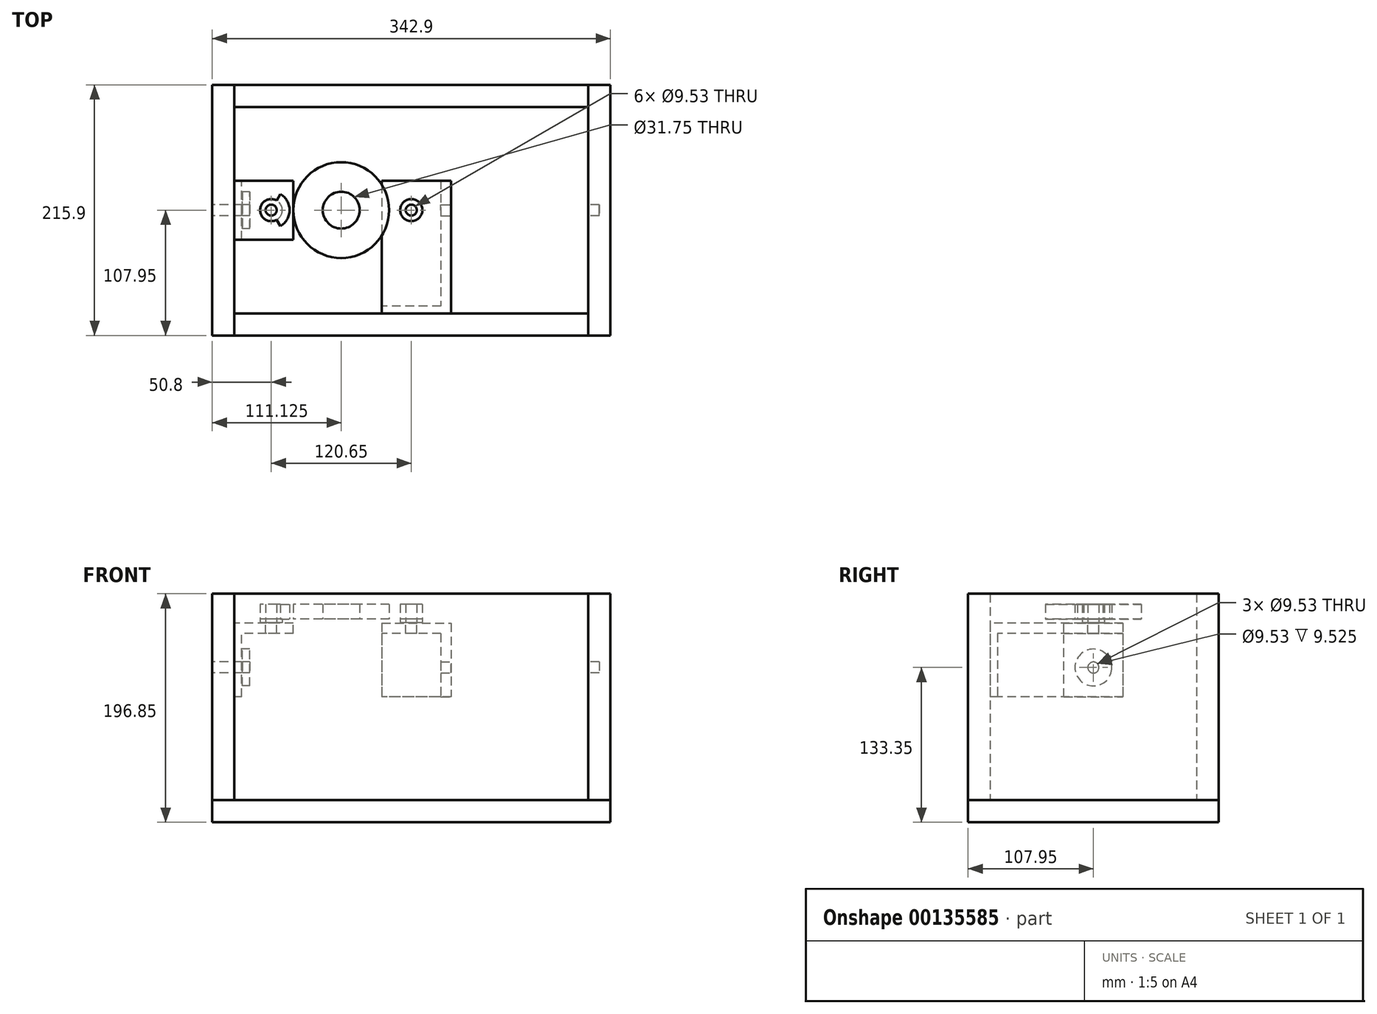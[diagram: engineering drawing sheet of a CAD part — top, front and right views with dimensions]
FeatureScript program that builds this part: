
annotation { "Feature Type Name" : "Feature", "Feature Type Description" : "" }
export const myFeature = defineFeature(function(context is Context, id is Id, definition is map)
    precondition{}
    {
        {
            var Q0;
            Q0=qCreatedBy(makeId("Top.planeOp"),FACE);
            var sketch = newSketch(context, id + "F0", { "sketchPlane" : qUnion([Q0])});
            skLineSegment(sketch, "E0.bottom", {"start": v(-152.4, 88.9) * mm, "end": v(152.4, 88.9) * mm});
            skLineSegment(sketch, "E0.top", {"start": v(-152.4, -88.9) * mm, "end": v(152.4, -88.9) * mm});
            skLineSegment(sketch, "E0.left", {"start": v(-152.4, 88.9) * mm, "end": v(-152.4, -88.9) * mm});
            skLineSegment(sketch, "E0.right", {"start": v(152.4, 88.9) * mm, "end": v(152.4, -88.9) * mm});
            skLineSegment(sketch, "E1.bottom", {"start": v(152.4, 107.95) * mm, "end": v(171.45, 107.95) * mm});
            skLineSegment(sketch, "E1.top", {"start": v(152.4, -107.95) * mm, "end": v(171.45, -107.95) * mm});
            skLineSegment(sketch, "E1.left", {"start": v(152.4, 107.95) * mm, "end": v(152.4, -107.95) * mm});
            skLineSegment(sketch, "E1.right", {"start": v(171.45, 107.95) * mm, "end": v(171.45, -107.95) * mm});
            skLineSegment(sketch, "E2", {"start": v(152.4, 107.95) * mm, "end": v(152.4, 0) * mm});
            skLineSegment(sketch, "E3", {"start": v(152.4, 88.9) * mm, "end": v(152.4, 0) * mm});
            skLineSegment(sketch, "E4.bottom", {"start": v(-171.45, 107.95) * mm, "end": v(-152.4, 107.95) * mm});
            skLineSegment(sketch, "E4.top", {"start": v(-171.45, -107.95) * mm, "end": v(-152.4, -107.95) * mm});
            skLineSegment(sketch, "E4.left", {"start": v(-171.45, 107.95) * mm, "end": v(-171.45, -107.95) * mm});
            skLineSegment(sketch, "E4.right", {"start": v(-152.4, 107.95) * mm, "end": v(-152.4, -107.95) * mm});
            skLineSegment(sketch, "E5", {"start": v(-171.45, 107.95) * mm, "end": v(-171.45, 0) * mm});
            skLineSegment(sketch, "E6", {"start": v(-152.4, 107.95) * mm, "end": v(-152.4, 0) * mm});
            skLineSegment(sketch, "E7", {"start": v(-152.4, 88.9) * mm, "end": v(-152.4, 0) * mm});
            skLineSegment(sketch, "E8.bottom", {"start": v(-152.4, 107.95) * mm, "end": v(152.4, 107.95) * mm});
            skLineSegment(sketch, "E8.left", {"start": v(-152.4, 107.95) * mm, "end": v(-152.4, 88.9) * mm});
            skLineSegment(sketch, "E8.right", {"start": v(152.4, 107.95) * mm, "end": v(152.4, 88.9) * mm});
            skLineSegment(sketch, "E9.bottom", {"start": v(-152.4, -107.95) * mm, "end": v(152.4, -107.95) * mm});
            skLineSegment(sketch, "E9.left", {"start": v(-152.4, -107.95) * mm, "end": v(-152.4, -88.9) * mm});
            skLineSegment(sketch, "E9.right", {"start": v(152.4, -107.95) * mm, "end": v(152.4, -88.9) * mm});
            skLineSegment(sketch, "E10", {"start": v(0, 88.9) * mm, "end": v(0, -88.9) * mm});
            skPoint(sketch, "E11", {"position": v(0, 0) * mm});
            skSolve(sketch);
        }
        {
            var Q0;
            Q0=makeQuery(id+"F0.imprint","IMPRINT",FACE,{"disambiguationData":[TD([[makeQuery(id+"F0.imprint","IMPRINT",EDGE,{"derivedFrom":sQuery(id+"F0.wireOp",EDGE,"E4.bottom")}),-1.0]])]});
            extrude(context, id + "F1", {"entities" : qUnion([Q0]), "depth" : 177.8 * mm});
        }
        {
            var Q0;
            Q0=makeQuery(id+"F0.imprint","IMPRINT",FACE,{"disambiguationData":[TD([[makeQuery(id+"F0.imprint","IMPRINT",EDGE,{"derivedFrom":sQuery(id+"F0.wireOp",EDGE,"E1.bottom")}),-1.0]])]});
            extrude(context, id + "F2", {"entities" : qUnion([Q0]), "depth" : 177.8 * mm});
        }
        {
            var Q0;
            Q0=makeQuery(id+"F0.imprint","IMPRINT",FACE,{"disambiguationData":[TD([[makeQuery(id+"F0.imprint","IMPRINT",EDGE,{"derivedFrom":sQuery(id+"F0.wireOp",EDGE,"E8.bottom")}),-1.0]])]});
            extrude(context, id + "F3", {"entities" : qUnion([Q0]), "depth" : 177.8 * mm});
        }
        {
            var Q0;
            Q0=makeQuery(id+"F0.imprint","IMPRINT",FACE,{"disambiguationData":[TD([[makeQuery(id+"F0.imprint","IMPRINT",EDGE,{"derivedFrom":sQuery(id+"F0.wireOp",EDGE,"E9.bottom")}),1.0]])]});
            extrude(context, id + "F4", {"entities" : qUnion([Q0]), "depth" : 177.8 * mm});
        }
        {
            var Q0;
            Q0=qCreatedBy(makeId("Top.planeOp"),FACE);
            var sketch = newSketch(context, id + "F5", { "sketchPlane" : qUnion([Q0])});
            skLineSegment(sketch, "E12.bottom", {"start": v(-171.45, -107.95) * mm, "end": v(171.45, -107.95) * mm});
            skLineSegment(sketch, "E12.top", {"start": v(-171.45, 107.95) * mm, "end": v(171.45, 107.95) * mm});
            skLineSegment(sketch, "E12.left", {"start": v(-171.45, -107.95) * mm, "end": v(-171.45, 107.95) * mm});
            skLineSegment(sketch, "E12.right", {"start": v(171.45, -107.95) * mm, "end": v(171.45, 107.95) * mm});
            skSolve(sketch);
        }
        {
            var Q0;
            Q0=qSketchRegion(id+"F5",true);
            extrude(context, id + "F6", {"entities" : qUnion([Q0]), "oppositeDirection" : true, "depth" : 19.05 * mm});
        }
        {
            var Q0;
            Q0=makeQuery(id+"F1.opExtrude","SWEPT_FACE",FACE,{"disambiguationData":[OSD([sQuery(id+"F0.wireOp",EDGE,"E4.left"),sQuery(id+"F0.wireOp",EDGE,"E5")])]});
            var sketch = newSketch(context, id + "F7", { "sketchPlane" : qUnion([Q0])});
            skLineSegment(sketch, "E13", {"start": v(0, 0) * mm, "end": v(0, 114.3) * mm, "construction": true});
            skCircle(sketch, "E14", {"center": v(0, 114.3) * mm, "radius": 4.76 * mm});
            skSolve(sketch);
        }
        {
            var Q0;
            Q0=makeQuery(id+"F7.imprint","IMPRINT",FACE,{"disambiguationData":[TD([[makeQuery(id+"F7.imprint","IMPRINT",EDGE,{"derivedFrom":sQuery(id+"F7.wireOp",EDGE,"E14")}),1.0]])]});
            var Q1;
            Q1=sQuery(id+"F7.wireOp",EDGE,"E14");
            extrude(context, id + "F8", {"entities" : qUnion([Q0]), "operationType" : NewBodyOperationType.REMOVE, "surfaceEntities" : qUnion([Q1]), "oppositeDirection" : true, "depth" : 19.05 * mm});
        }
        {
            var Q0;
            Q0=makeQuery(id+"F2.opExtrude","SWEPT_FACE",FACE,{"disambiguationData":[OSD([sQuery(id+"F0.wireOp",EDGE,"E1.left"),sQuery(id+"F0.wireOp",EDGE,"E3"),sQuery(id+"F0.wireOp",EDGE,"E8.right"),sQuery(id+"F0.wireOp",EDGE,"E9.right")])]});
            var sketch = newSketch(context, id + "F9", { "sketchPlane" : qUnion([Q0])});
            skCircle(sketch, "E15.0", {"center": v(0, 114.3) * mm, "radius": 4.76 * mm});
            skSolve(sketch);
        }
        {
            var Q0;
            Q0=makeQuery(id+"F9.imprint","IMPRINT",FACE,{"disambiguationData":[TD([[makeQuery(id+"F9.imprint","IMPRINT",EDGE,{"derivedFrom":sQuery(id+"F9.wireOp",EDGE,"E15.0")}),1.0]])]});
            extrude(context, id + "F10", {"entities" : qUnion([Q0]), "operationType" : NewBodyOperationType.REMOVE, "oppositeDirection" : true, "depth" : 9.52 * mm});
        }
        {
            var Q0;
            Q0=makeQuery(id+"F1.opExtrude","SWEPT_FACE",FACE,{"disambiguationData":[OSD([sQuery(id+"F0.wireOp",EDGE,"E4.right"),sQuery(id+"F0.wireOp",EDGE,"E7"),sQuery(id+"F0.wireOp",EDGE,"E8.left"),sQuery(id+"F0.wireOp",EDGE,"E9.left")])]});
            var sketch = newSketch(context, id + "F11", { "sketchPlane" : qUnion([Q0])});
            skCircle(sketch, "E16.0", {"center": v(0, 114.3) * mm, "radius": 4.76 * mm, "construction": true});
            skLineSegment(sketch, "E17", {"start": v(0, 114.3) * mm, "end": v(-25.4, 114.3) * mm, "construction": true});
            skLineSegment(sketch, "E18", {"start": v(0, 114.3) * mm, "end": v(25.4, 114.3) * mm, "construction": true});
            skLineSegment(sketch, "E19", {"start": v(-25.4, 114.3) * mm, "end": v(-25.4, 88.9) * mm, "construction": true});
            skLineSegment(sketch, "E20", {"start": v(-25.4, 114.3) * mm, "end": v(-25.4, 152.4) * mm, "construction": true});
            skLineSegment(sketch, "E21.MirrorCS", {"start": v(25.4, 114.3) * mm, "end": v(25.4, 152.4) * mm, "construction": true});
            skLineSegment(sketch, "E22.MirrorCS", {"start": v(25.4, 114.3) * mm, "end": v(25.4, 88.9) * mm, "construction": true});
            skLineSegment(sketch, "E23", {"start": v(-25.4, 152.4) * mm, "end": v(25.4, 152.4) * mm, "construction": true});
            skLineSegment(sketch, "E24", {"start": v(-25.4, 88.9) * mm, "end": v(25.4, 88.9) * mm, "construction": true});
            skLineSegment(sketch, "E25.bottom", {"start": v(-25.4, 88.9) * mm, "end": v(25.4, 88.9) * mm});
            skLineSegment(sketch, "E25.top", {"start": v(-25.4, 152.4) * mm, "end": v(25.4, 152.4) * mm});
            skLineSegment(sketch, "E25.left", {"start": v(-25.4, 88.9) * mm, "end": v(-25.4, 152.4) * mm});
            skLineSegment(sketch, "E25.right", {"start": v(25.4, 88.9) * mm, "end": v(25.4, 152.4) * mm});
            skLineSegment(sketch, "E26", {"start": v(-25.4, 152.4) * mm, "end": v(-25.4, 143.5) * mm, "construction": true});
            skLineSegment(sketch, "E27", {"start": v(-25.4, 143.5) * mm, "end": v(25.4, 143.5) * mm});
            skSolve(sketch);
        }
        {
            var Q0;
            {var subQ2=sQuery(id+"F11.wireOp",EDGE,"E25.bottom");Q0=makeQuery(id+"F11.imprint","IMPRINT",FACE,{"disambiguationData":[TD([[makeQuery(id+"F11.imprint","IMPRINT",EDGE,{"derivedFrom":subQ2}),1.0]])]});}
            extrude(context, id + "F12", {"entities" : qUnion([Q0]), "operationType" : NewBodyOperationType.ADD, "depth" : 6.35 * mm});
        }
        {
            var Q0;
            {var subQ0=sQuery(id+"F11.wireOp",EDGE,"E25.top");Q0=makeQuery(id+"F11.imprint","IMPRINT",FACE,{"disambiguationData":[TD([[makeQuery(id+"F11.imprint","IMPRINT",EDGE,{"derivedFrom":subQ0}),-1.0]])]});}
            extrude(context, id + "F13", {"entities" : qUnion([Q0]), "operationType" : NewBodyOperationType.ADD, "depth" : 50.8 * mm});
        }
        {
            var Q0;
            Q0=makeQuery(id+"F12.opExtrude","CAP_FACE",FACE,{"disambiguationData":[OSD([sQuery(id+"F7.wireOp",EDGE,"E14"),sQuery(id+"F11.wireOp",EDGE,"E25.bottom"),sQuery(id+"F11.wireOp",EDGE,"E25.left"),sQuery(id+"F11.wireOp",EDGE,"E25.right"),sQuery(id+"F11.wireOp",EDGE,"E27")])],"isStart":false});
            var sketch = newSketch(context, id + "F14", { "sketchPlane" : qUnion([Q0])});
            skCircle(sketch, "E28.0", {"center": v(0, 114.3) * mm, "radius": 4.76 * mm, "construction": true});
            skCircle(sketch, "E29", {"center": v(0, 114.3) * mm, "radius": 15.88 * mm});
            skCircle(sketch, "E30", {"center": v(0, 82.55) * mm, "radius": 4.76 * mm});
            skCircle(sketch, "E31", {"center": v(0, 82.55) * mm, "radius": 15.88 * mm});
            skLineSegment(sketch, "E32", {"start": v(0, 114.3) * mm, "end": v(0, 82.55) * mm, "construction": true});
            skLineSegment(sketch, "E33", {"start": v(-4.76, 114.33) * mm, "end": v(4.76, 114.33) * mm, "construction": true});
            skLineSegment(sketch, "E34", {"start": v(0, 82.55) * mm, "end": v(0, 50.8) * mm, "construction": true});
            skCircle(sketch, "E35", {"center": v(0, 50.8) * mm, "radius": 4.76 * mm});
            skCircle(sketch, "E36", {"center": v(0, 50.8) * mm, "radius": 15.88 * mm});
            skSolve(sketch);
        }
        {
            var Q0;
            Q0=makeQuery(id+"F14.imprint","IMPRINT",FACE,{"disambiguationData":[TD([[makeQuery(id+"F14.imprint","IMPRINT",EDGE,{"derivedFrom":sQuery(id+"F14.wireOp",EDGE,"E29")}),1.0]])]});
            var Q1;
            Q1=makeQuery(id+"F14.imprint","IMPRINT",FACE,{"disambiguationData":[TD([[makeQuery(id+"F14.imprint","IMPRINT",EDGE,{"derivedFrom":sQuery(id+"F14.wireOp",EDGE,"wCvrm9ek-Vla4-kLHZ-fckN-ywa5dthquzuu")}),-1.0]])]});
            var Q2;
            {var subQ0=sQuery(id+"F14.wireOp",EDGE,"TcqK1HJN-8NVO-TRNo-AAgI-cdNEvH082vga");var subQ1=makeQuery(id+"F12.opExtrude","CAP_EDGE",EDGE,{"disambiguationData":[OSD([sQuery(id+"F11.wireOp",EDGE,"E25.bottom")])],"isStart":false});var subQ2=makeQuery(id+"F14.imprint","INTERSECT",VERTEX,{"disambiguationData":[OD(0.0)],"derivedFrom":[subQ1,subQ0]});Q2=makeQuery(id+"F14.imprint","IMPRINT",FACE,{"disambiguationData":[TD([[makeQuery(id+"F14.imprint","IMPRINT",EDGE,{"disambiguationData":[TD([[subQ2,1.0]])],"derivedFrom":subQ0}),1.0]])]});}
            var Q3;
            Q3=makeQuery(id+"F14.imprint","IMPRINT",FACE,{"disambiguationData":[TD([[makeQuery(id+"F14.imprint","IMPRINT",EDGE,{"derivedFrom":sQuery(id+"F14.wireOp",EDGE,"75hCYlV7-Y9NR-4qaa-elEN-DsRLMhdoIlUx")}),1.0]])]});
            extrude(context, id + "F15", {"entities" : qUnion([Q0, Q1, Q2, Q3]), "depth" : 6.86 * mm, "hasSecondDirection" : true, "secondDirectionOppositeDirection" : false, "secondDirectionDepth" : 0.5 * mm});
        }
        {
            var Q0;
            Q0=makeQuery(id+"F13.opExtrude","SWEPT_FACE",FACE,{"disambiguationData":[OSD([sQuery(id+"F11.wireOp",EDGE,"E25.top")])]});
            var sketch = newSketch(context, id + "F16", { "sketchPlane" : qUnion([Q0])});
            skLineSegment(sketch, "E37", {"start": v(-152.4, 0) * mm, "end": v(-101.6, 0) * mm, "construction": true});
            skLineSegment(sketch, "E38", {"start": v(-101.6, 0) * mm, "end": v(-127, 0) * mm, "construction": true});
            skLineSegment(sketch, "E39", {"start": v(-127, 0) * mm, "end": v(-114.3, 0) * mm, "construction": true});
            skLineSegment(sketch, "E40", {"start": v(-114.3, 0) * mm, "end": v(-120.65, 0) * mm, "construction": true});
            skCircle(sketch, "E41", {"center": v(-120.65, 0) * mm, "radius": 4.76 * mm});
            skSolve(sketch);
        }
        {
            var Q0;
            Q0=makeQuery(id+"F16.imprint","IMPRINT",FACE,{"disambiguationData":[TD([[makeQuery(id+"F16.imprint","IMPRINT",EDGE,{"derivedFrom":sQuery(id+"F16.wireOp",EDGE,"E41")}),1.0]])]});
            var Q1;
            Q1=sQuery(id+"F16.wireOp",EDGE,"E41");
            extrude(context, id + "F17", {"entities" : qUnion([Q0]), "operationType" : NewBodyOperationType.REMOVE, "surfaceEntities" : qUnion([Q1]), "oppositeDirection" : true, "depth" : 25.4 * mm});
        }
        {
            var Q0;
            Q0=makeQuery(id+"F4.opExtrude","SWEPT_FACE",FACE,{"disambiguationData":[OSD([sQuery(id+"F0.wireOp",EDGE,"E0.top")])]});
            var sketch = newSketch(context, id + "F18", { "sketchPlane" : qUnion([Q0])});
            skLineSegment(sketch, "E42.0.0", {"start": v(152.4, 88.9) * mm, "end": v(152.4, 152.4) * mm, "construction": true});
            skLineSegment(sketch, "E42.0.1", {"start": v(152.4, 152.4) * mm, "end": v(101.6, 152.4) * mm, "construction": true});
            skLineSegment(sketch, "E42.0.2", {"start": v(101.6, 152.4) * mm, "end": v(101.6, 143.5) * mm, "construction": true});
            skLineSegment(sketch, "E42.0.3", {"start": v(101.6, 143.5) * mm, "end": v(146.05, 143.5) * mm, "construction": true});
            skLineSegment(sketch, "E42.0.4", {"start": v(146.05, 143.5) * mm, "end": v(146.05, 88.9) * mm, "construction": true});
            skLineSegment(sketch, "E42.0.5", {"start": v(146.05, 88.9) * mm, "end": v(152.4, 88.9) * mm, "construction": true});
            skLineSegment(sketch, "E43", {"start": v(152.4, 152.4) * mm, "end": v(-25.4, 152.4) * mm, "construction": true});
            skLineSegment(sketch, "E44.bottom", {"start": v(-25.4, 152.4) * mm, "end": v(25.4, 152.4) * mm});
            skLineSegment(sketch, "E44.top", {"start": v(-25.4, 88.9) * mm, "end": v(25.4, 88.9) * mm});
            skLineSegment(sketch, "E44.left", {"start": v(-25.4, 152.4) * mm, "end": v(-25.4, 88.9) * mm});
            skLineSegment(sketch, "E44.right", {"start": v(25.4, 152.4) * mm, "end": v(25.4, 88.9) * mm});
            skLineSegment(sketch, "E45.top", {"start": v(-25.4, 143.5) * mm, "end": v(25.4, 143.5) * mm});
            skLineSegment(sketch, "E45.left", {"start": v(-25.4, 152.4) * mm, "end": v(-25.4, 143.5) * mm});
            skLineSegment(sketch, "E45.right", {"start": v(25.4, 152.4) * mm, "end": v(25.4, 143.5) * mm});
            skLineSegment(sketch, "E46.bottom", {"start": v(-25.4, 152.4) * mm, "end": v(-34.3, 152.4) * mm});
            skLineSegment(sketch, "E46.top", {"start": v(-25.4, 88.9) * mm, "end": v(-34.3, 88.9) * mm});
            skLineSegment(sketch, "E46.right", {"start": v(-34.3, 152.4) * mm, "end": v(-34.3, 88.9) * mm});
            skSolve(sketch);
        }
        {
            var Q0;
            {var subQ0=sQuery(id+"F18.wireOp",EDGE,"E44.top");Q0=makeQuery(id+"F18.imprint","IMPRINT",FACE,{"disambiguationData":[TD([[makeQuery(id+"F18.imprint","IMPRINT",EDGE,{"derivedFrom":subQ0}),1.0]])]});}
            extrude(context, id + "F19", {"entities" : qUnion([Q0]), "operationType" : NewBodyOperationType.ADD, "depth" : 6.35 * mm});
        }
        {
            var Q0;
            {var subQ3=sQuery(id+"F18.wireOp",EDGE,"E46.bottom");Q0=makeQuery(id+"F18.imprint","IMPRINT",FACE,{"disambiguationData":[TD([[makeQuery(id+"F18.imprint","IMPRINT",EDGE,{"derivedFrom":subQ3}),1.0]])]});}
            var Q1;
            {var subQ0=sQuery(id+"F18.wireOp",EDGE,"E44.bottom");Q1=makeQuery(id+"F18.imprint","IMPRINT",FACE,{"disambiguationData":[TD([[makeQuery(id+"F18.imprint","IMPRINT",EDGE,{"derivedFrom":subQ0}),-1.0]])]});}
            extrude(context, id + "F20", {"entities" : qUnion([Q0, Q1]), "operationType" : NewBodyOperationType.ADD, "depth" : 114.3 * mm});
        }
        {
            var Q0;
            Q0=makeQuery(id+"F20.opExtrude","SWEPT_FACE",FACE,{"disambiguationData":[OSD([sQuery(id+"F18.wireOp",EDGE,"E46.right")])]});
            var sketch = newSketch(context, id + "F21", { "sketchPlane" : qUnion([Q0])});
            skCircle(sketch, "E47.0", {"center": v(0, 114.3) * mm, "radius": 4.76 * mm});
            skSolve(sketch);
        }
        {
            var Q0;
            Q0=makeQuery(id+"F21.imprint","IMPRINT",FACE,{"disambiguationData":[TD([[makeQuery(id+"F21.imprint","IMPRINT",EDGE,{"derivedFrom":sQuery(id+"F21.wireOp",EDGE,"E47.0")}),1.0]])]});
            var Q1;
            Q1=sQuery(id+"F21.wireOp",EDGE,"E47.0");
            extrude(context, id + "F22", {"entities" : qUnion([Q0]), "operationType" : NewBodyOperationType.REMOVE, "surfaceEntities" : qUnion([Q1]), "oppositeDirection" : true, "depth" : 25.4 * mm});
        }
        {
            var Q0;
            Q0=makeQuery(id+"F20.opExtrude","SWEPT_FACE",FACE,{"disambiguationData":[OSD([sQuery(id+"F18.wireOp",EDGE,"E44.bottom"),sQuery(id+"F18.wireOp",EDGE,"E46.bottom")])]});
            var sketch = newSketch(context, id + "F23", { "sketchPlane" : qUnion([Q0])});
            skCircle(sketch, "E48.0", {"center": v(-120.65, 0) * mm, "radius": 4.76 * mm, "construction": true});
            skLineSegment(sketch, "E49", {"start": v(-120.65, 0) * mm, "end": v(0, 0) * mm, "construction": true});
            skCircle(sketch, "E50", {"center": v(0, 0) * mm, "radius": 4.76 * mm});
            skSolve(sketch);
        }
        {
            var Q0;
            Q0=makeQuery(id+"F23.imprint","IMPRINT",FACE,{"disambiguationData":[TD([[makeQuery(id+"F23.imprint","IMPRINT",EDGE,{"derivedFrom":sQuery(id+"F23.wireOp",EDGE,"E50")}),1.0]])]});
            var Q1;
            Q1=sQuery(id+"F23.wireOp",EDGE,"E50");
            extrude(context, id + "F24", {"entities" : qUnion([Q0]), "operationType" : NewBodyOperationType.REMOVE, "surfaceEntities" : qUnion([Q1]), "oppositeDirection" : true, "depth" : 25.4 * mm});
        }
        {
            var Q0;
            Q0=makeQuery(id+"F20.opExtrude","SWEPT_FACE",FACE,{"disambiguationData":[OSD([sQuery(id+"F18.wireOp",EDGE,"E44.bottom"),sQuery(id+"F18.wireOp",EDGE,"E46.bottom")])]});
            var sketch = newSketch(context, id + "F25", { "sketchPlane" : qUnion([Q0])});
            skCircle(sketch, "E51.0", {"center": v(-120.65, 0) * mm, "radius": 4.76 * mm});
            skCircle(sketch, "E52.0", {"center": v(0, 0) * mm, "radius": 4.76 * mm});
            skLineSegment(sketch, "E53", {"start": v(-120.65, 0) * mm, "end": v(0, 0) * mm, "construction": true});
            skLineSegment(sketch, "E54", {"start": v(-60.32, 0) * mm, "end": v(-60.32, 25.4) * mm, "construction": true});
            skCircle(sketch, "E55", {"center": v(0, 0) * mm, "radius": 9.53 * mm});
            skCircle(sketch, "E56.MirrorC", {"center": v(-120.65, 0) * mm, "radius": 9.53 * mm});
            skSolve(sketch);
        }
        {
            var Q0;
            Q0=makeQuery(id+"F25.imprint","IMPRINT",FACE,{"disambiguationData":[TD([[makeQuery(id+"F25.imprint","IMPRINT",EDGE,{"derivedFrom":sQuery(id+"F25.wireOp",EDGE,"E51.0")}),-1.0]])]});
            var Q1;
            Q1=makeQuery(id+"F25.imprint","IMPRINT",FACE,{"disambiguationData":[TD([[makeQuery(id+"F25.imprint","IMPRINT",EDGE,{"derivedFrom":sQuery(id+"F25.wireOp",EDGE,"E52.0")}),-1.0]])]});
            var Q2;
            Q2=sQuery(id+"F25.wireOp",EDGE,"E56.MirrorC");
            var Q3;
            Q3=sQuery(id+"F25.wireOp",EDGE,"E55");
            extrude(context, id + "F26", {"entities" : qUnion([Q0, Q1]), "operationType" : NewBodyOperationType.ADD, "surfaceEntities" : qUnion([Q2, Q3]), "depth" : 3.68 * mm, "hasSecondDirection" : true, "secondDirectionOppositeDirection" : false, "secondDirectionDepth" : 0.5 * mm});
        }
        {
            var Q0;
            Q0=makeQuery(id+"F26.opExtrude","CAP_FACE",FACE,{"disambiguationData":[OSD([sQuery(id+"F25.wireOp",EDGE,"E51.0"),sQuery(id+"F25.wireOp",EDGE,"E56.MirrorC")])],"isStart":false});
            var sketch = newSketch(context, id + "F27", { "sketchPlane" : qUnion([Q0])});
            skCircle(sketch, "E57.0", {"center": v(-120.65, 0) * mm, "radius": 4.76 * mm, "construction": true});
            skCircle(sketch, "E58.0", {"center": v(0, 0) * mm, "radius": 4.76 * mm, "construction": true});
            skLineSegment(sketch, "E59", {"start": v(-120.65, 0) * mm, "end": v(0, 0) * mm, "construction": true});
            skLineSegment(sketch, "E60", {"start": v(-60.32, 0) * mm, "end": v(-60.32, 25.4) * mm, "construction": true});
            skArc(sketch, "E61", {"start": v(-112.71, -13.75) * mm, "mid": v(-104.77, 0) * mm, "end": v(-112.71, 13.75) * mm});
            skLineSegment(sketch, "E62", {"start": v(-120.65, 0) * mm, "end": v(-120.65, 9.53) * mm, "construction": true});
            skLineSegment(sketch, "E63", {"start": v(-120.65, 0) * mm, "end": v(-120.65, -9.53) * mm, "construction": true});
            skLineSegment(sketch, "E64", {"start": v(-120.65, 0) * mm, "end": v(-112.71, 13.75) * mm, "construction": true});
            skLineSegment(sketch, "E65", {"start": v(-120.65, 0) * mm, "end": v(-112.71, -13.75) * mm, "construction": true});
            skLineSegment(sketch, "E66", {"start": v(-112.71, -13.75) * mm, "end": v(-115.89, -8.25) * mm});
            skLineSegment(sketch, "E67", {"start": v(-112.71, 13.75) * mm, "end": v(-115.89, 8.25) * mm});
            skLineSegment(sketch, "E68.MirrorCS", {"start": v(0, 0) * mm, "end": v(-7.94, -13.75) * mm, "construction": true});
            skLineSegment(sketch, "E69.MirrorCS", {"start": v(0, 0) * mm, "end": v(-7.94, 13.75) * mm, "construction": true});
            skArc(sketch, "E70.MirrorCS", {"start": v(-7.94, -13.75) * mm, "mid": v(-15.88, 0) * mm, "end": v(-7.94, 13.75) * mm});
            skCircle(sketch, "E71.0", {"center": v(0, 0) * mm, "radius": 9.53 * mm});
            skLineSegment(sketch, "E72", {"start": v(-7.94, 13.75) * mm, "end": v(-4.76, 8.25) * mm});
            skLineSegment(sketch, "E73", {"start": v(-7.94, -13.75) * mm, "end": v(-4.76, -8.25) * mm});
            skCircle(sketch, "E74", {"center": v(0, 0) * mm, "radius": 4.76 * mm});
            skCircle(sketch, "E75", {"center": v(-60.32, 0) * mm, "radius": 41.28 * mm});
            skCircle(sketch, "E76", {"center": v(-60.32, 0) * mm, "radius": 15.88 * mm});
            skSolve(sketch);
        }
        {
            var Q0;
            Q0=makeQuery(id+"F27.imprint","IMPRINT",FACE,{"disambiguationData":[TD([[makeQuery(id+"F27.imprint","IMPRINT",EDGE,{"derivedFrom":sQuery(id+"F27.wireOp",EDGE,"E61")}),1.0]])]});
            var Q1;
            Q1=makeQuery(id+"F27.imprint","IMPRINT",FACE,{"disambiguationData":[TD([[makeQuery(id+"F27.imprint","IMPRINT",EDGE,{"derivedFrom":sQuery(id+"F27.wireOp",EDGE,"E74")}),-1.0]])]});
            var Q2;
            Q2=makeQuery(id+"F27.imprint","IMPRINT",FACE,{"disambiguationData":[TD([[makeQuery(id+"F27.imprint","IMPRINT",EDGE,{"derivedFrom":sQuery(id+"F27.wireOp",EDGE,"E70.MirrorCS")}),-1.0]])]});
            var Q3;
            Q3=makeQuery(id+"F27.imprint","IMPRINT",FACE,{"disambiguationData":[TD([[makeQuery(id+"F27.imprint","IMPRINT",EDGE,{"derivedFrom":makeQuery(id+"F26.opExtrude","CAP_EDGE",EDGE,{"disambiguationData":[OSD([sQuery(id+"F25.wireOp",EDGE,"E51.0")])],"isStart":false})}),-1.0]])]});
            var Q4;
            Q4=makeQuery(id+"F27.imprint","IMPRINT",FACE,{"disambiguationData":[TD([[makeQuery(id+"F27.imprint","IMPRINT",EDGE,{"derivedFrom":sQuery(id+"F27.wireOp",EDGE,"E75")}),1.0]])]});
            extrude(context, id + "F28", {"entities" : qUnion([Q0, Q1, Q2, Q3, Q4]), "depth" : 12.7 * mm});
        }
        {
            var Q0;
            Q0=makeQuery(id+"F1.opExtrude","SWEPT_FACE",FACE,{"disambiguationData":[OSD([sQuery(id+"F0.wireOp",EDGE,"E4.left"),sQuery(id+"F0.wireOp",EDGE,"E5")])]});
            var sketch = newSketch(context, id + "F29", { "sketchPlane" : qUnion([Q0])});
            skCircle(sketch, "E77.0", {"center": v(0, 114.3) * mm, "radius": 4.76 * mm, "construction": true});
            skCircle(sketch, "E78", {"center": v(0, 114.3) * mm, "radius": 4.5 * mm});
            skSolve(sketch);
        }
        {
            var Q0;
            Q0=sQuery(id+"F29.wireOp",EDGE,"E78");
            extrude(context, id + "F30", {"bodyType" : ToolBodyType.SURFACE, "surfaceEntities" : qUnion([Q0]), "oppositeDirection" : true, "depth" : 333.38 * mm});
        }
    });
